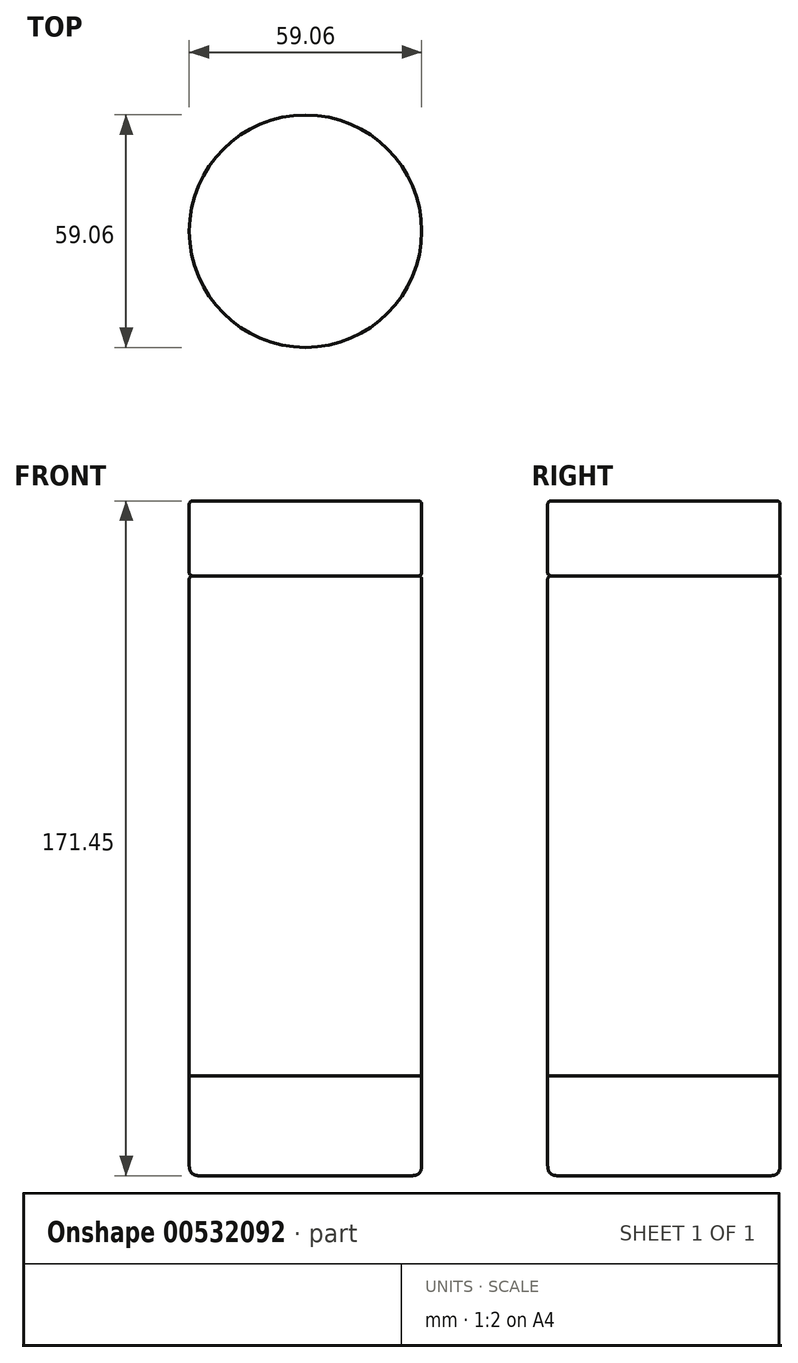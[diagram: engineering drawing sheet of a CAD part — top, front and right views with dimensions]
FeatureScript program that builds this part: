
annotation { "Feature Type Name" : "Feature", "Feature Type Description" : "" }
export const myFeature = defineFeature(function(context is Context, id is Id, definition is map)
    precondition{}
    {
        {
            var Q0;
            Q0=qCreatedBy(makeId("Front.planeOp"),FACE);
            var sketch = newSketch(context, id + "F0", { "sketchPlane" : qUnion([Q0])});
            skLineSegment(sketch, "E0", {"start": v(0, 110.75) * mm, "end": v(0, 0) * mm, "construction": true});
            skLineSegment(sketch, "E1", {"start": v(0, 0) * mm, "end": v(29.53, 0) * mm});
            skLineSegment(sketch, "E2", {"start": v(29.53, 0) * mm, "end": v(29.53, 25.4) * mm});
            skLineSegment(sketch, "E3", {"start": v(29.53, 25.4) * mm, "end": v(0, 25.4) * mm});
            skLineSegment(sketch, "E4", {"start": v(0, 25.4) * mm, "end": v(0, 0) * mm});
            skSolve(sketch);
        }
        {
            var Q0;
            Q0=makeQuery(id+"F0.imprint","IMPRINT",FACE,{"disambiguationData":[TD([[makeQuery(id+"F0.imprint","IMPRINT",EDGE,{"derivedFrom":sQuery(id+"F0.wireOp",EDGE,"E1")}),1.0]])]});
            var Q1;
            Q1=sQuery(id+"F0.wireOp",EDGE,"E0");
            revolve(context, id + "F1", {"entities" : qUnion([Q0]), "axis" : qUnion([Q1]), "revolveType" : RevolveType.FULL});
        }
        {
            var Q0;
            Q0=makeQuery(id+"F1.opRevolve","SWEPT_EDGE",EDGE,{"disambiguationData":[OSD([sQuery(id+"F0.wireOp",EDGE,"E1"),sQuery(id+"F0.wireOp",EDGE,"E2")])]});
            fillet(context, id + "F2", {"entities" : qUnion([Q0]), "radius" : 2.54 * mm, "tangentPropagation" : true, "rho" : 0.5, "crossSection" : FilletCrossSection.CONIC, "allowEdgeOverflow" : false});
        }
        {
            var Q0;
            Q0=makeQuery(id+"F1.opRevolve","SWEPT_FACE",FACE,{"disambiguationData":[OSD([sQuery(id+"F0.wireOp",EDGE,"E3")])]});
            var sketch = newSketch(context, id + "F3", { "sketchPlane" : qUnion([Q0])});
            skCircle(sketch, "E5.0.0", {"center": v(0, 0) * mm, "radius": 29.53 * mm});
            skSolve(sketch);
        }
        {
            var Q0;
            Q0 = qSketchRegion(id + "F3", true);
            extrude(context, id + "F4", {"entities" : qUnion([Q0]), "depth" : 127 * mm, "offsetDistance" : 25.4 * mm});
        }
        {
            var Q0;
            Q0=makeQuery(id+"F4.opExtrude","CAP_FACE",FACE,{"disambiguationData":[OSD([sQuery(id+"F3.wireOp",EDGE,"E5.0.0")])],"isStart":false});
            var sketch = newSketch(context, id + "F5", { "sketchPlane" : qUnion([Q0])});
            skCircle(sketch, "E6.0.0", {"center": v(0, 0) * mm, "radius": 29.53 * mm});
            skSolve(sketch);
        }
        {
            var Q0;
            Q0 = qSketchRegion(id + "F5", true);
            extrude(context, id + "F6", {"entities" : qUnion([Q0]), "depth" : 19.05 * mm, "offsetDistance" : 25.4 * mm});
        }
        {
            var Q0;
            Q0=makeQuery(id+"F4.opExtrude","CAP_EDGE",EDGE,{"disambiguationData":[OSD([sQuery(id+"F3.wireOp",EDGE,"E5.0.0")])],"isStart":false});
            fillet(context, id + "F7", {"entities" : qUnion([Q0]), "radius" : 0.81 * mm, "tangentPropagation" : true, "allowEdgeOverflow" : false});
        }
        {
            var Q0;
            Q0=makeQuery(id+"F6.opExtrude","CAP_EDGE",EDGE,{"disambiguationData":[OSD([sQuery(id+"F5.wireOp",EDGE,"E6.0.0")])],"isStart":true});
            fillet(context, id + "F8", {"entities" : qUnion([Q0]), "radius" : 0.81 * mm, "tangentPropagation" : true, "allowEdgeOverflow" : false});
        }
        {
            var Q0;
            Q0=makeQuery(id+"F6.opExtrude","CAP_EDGE",EDGE,{"disambiguationData":[OSD([sQuery(id+"F5.wireOp",EDGE,"E6.0.0")])],"isStart":false});
            fillet(context, id + "F9", {"entities" : qUnion([Q0]), "radius" : 0.81 * mm, "tangentPropagation" : true, "allowEdgeOverflow" : false});
        }
    });
